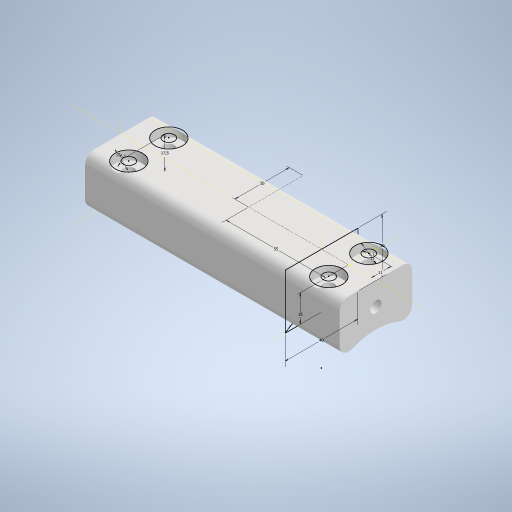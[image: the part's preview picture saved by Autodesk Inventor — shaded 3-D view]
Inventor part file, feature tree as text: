
AUTODESK INVENTOR PART (.ipt)
format: ipt  version: 2024.2 (Build 282272000, 272)  size: 346,112 bytes
history: native  units: mm
features: extrude x7, sketch x5, hole x2, other x1, fillet x1
ambient origin geometry x8: Origin, YZ Plane, XZ Plane, XY Plane, X Axis, Y Axis, Z Axis, Center Point
bodies: Body1 (feature_tree)
feature tree (16):
  other  "Bryła1"
  extrude  "Wyciągnięcie proste1"  Depth=30.0mm
  sketch  "Szkic2"
  extrude  "Wyciągnięcie proste2"  Depth=40.0mm
  extrude  "Wyciągnięcie proste3"  Depth=30.0mm TaperAngle=0.0deg
  fillet  "Zaokrąglenie1"  Radius=40.0mm
  sketch  "Szkic3"
  extrude  "Wyciągnięcie proste4"  Depth=30.0mm
  extrude  "Wyciągnięcie proste5"  Depth=15.0mm
  extrude  "Wyciągnięcie proste6"  Depth=110.0mm TaperAngle=0.0deg
  sketch  "Szkic5"
  sketch  "Szkic6"
  extrude  "Wyciągnięcie proste7"  TaperAngle=0.0deg  [1 undecoded]
  hole  "Otwór1"  [1 undecoded]
  hole  "Otwór2"  [1 undecoded]
  sketch  "Szkic1"
note: 3 required parameter values undecoded (feature->parameter linkage not recoverable at this tier; creation-order binding heuristic only, values carry confidence <= 0.55)
